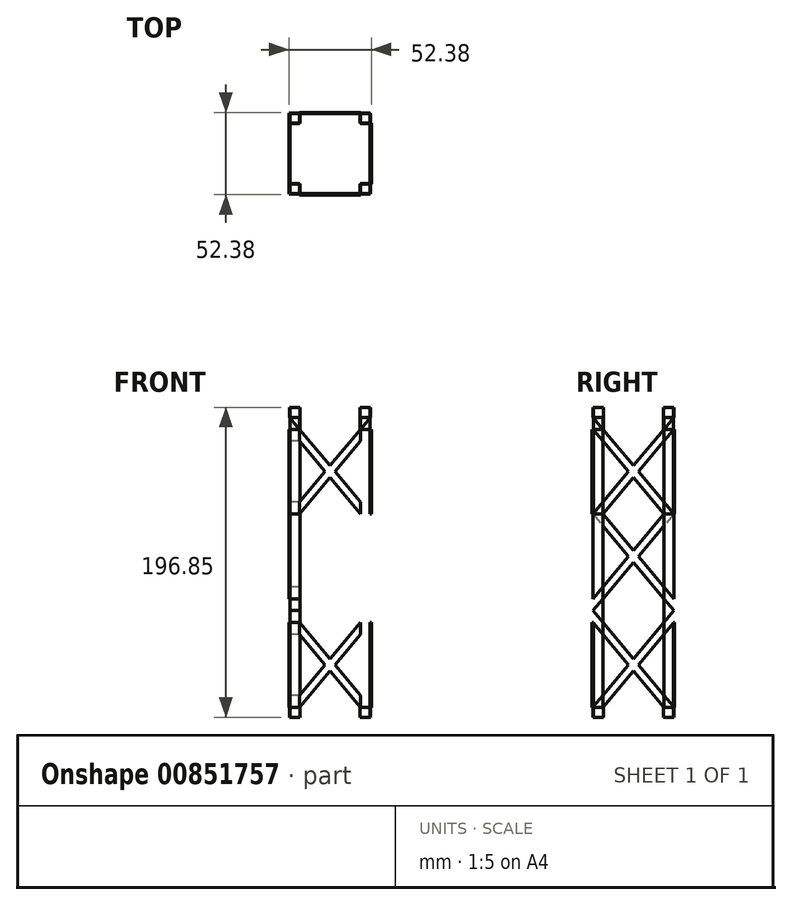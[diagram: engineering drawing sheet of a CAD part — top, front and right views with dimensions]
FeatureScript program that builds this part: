
annotation { "Feature Type Name" : "Feature", "Feature Type Description" : "" }
export const myFeature = defineFeature(function(context is Context, id is Id, definition is map)
    precondition{}
    {
        {
            var Q0;
            Q0=qCreatedBy(makeId("Front.planeOp"),FACE);
            var sketch = newSketch(context, id + "F0", { "sketchPlane" : qUnion([Q0])});
            skLineSegment(sketch, "E0", {"start": v(0, 0) * mm, "end": v(0, 196.85) * mm, "construction": true});
            skSolve(sketch);
        }
        {
            var Q0;
            Q0=qCreatedBy(makeId("Top.planeOp"),FACE);
            var sketch = newSketch(context, id + "F1", { "sketchPlane" : qUnion([Q0])});
            skLineSegment(sketch, "E1", {"start": v(0, 0) * mm, "end": v(-152.4, 0) * mm, "construction": true});
            skLineSegment(sketch, "E2", {"start": v(0, 0) * mm, "end": v(0, 152.4) * mm, "construction": true});
            skPoint(sketch, "E3", {"position": v(-25.4, 25.4) * mm});
            skPoint(sketch, "E4.MirrorP", {"position": v(-25.4, -25.4) * mm});
            skPoint(sketch, "E5.MirrorP", {"position": v(25.4, 25.4) * mm});
            skPoint(sketch, "E6.MirrorP", {"position": v(25.4, -25.4) * mm});
            skLineSegment(sketch, "E7", {"start": v(-25.4, 25.4) * mm, "end": v(-25.4, -25.4) * mm});
            skSolve(sketch);
        }
        {
            var Q0;
            Q0=sQuery(id+"F1.wireOp",EDGE,"E7");
            var Q1;
            Q1=qCreatedBy(makeId("Top.planeOp"),FACE);
            cPlane(context, id + "F2", {"entities" : qUnion([Q0, Q1]), "cplaneType" : CPlaneType.LINE_ANGLE, "offset" : 25.4 * mm, "angle" : 90 * degree, "width" : 152.4 * mm, "height" : 152.4 * mm});
        }
        {
            var Q0;
            Q0=qCreatedBy(id+"F2.planeOp",FACE);
            var sketch = newSketch(context, id + "F3", { "sketchPlane" : qUnion([Q0])});
            skLineSegment(sketch, "E8", {"start": v(-25.74, 0) * mm, "end": v(-25.74, 196.85) * mm});
            skLineSegment(sketch, "E9", {"start": v(-25.74, 196.85) * mm, "end": v(-19.39, 196.85) * mm});
            skLineSegment(sketch, "E10", {"start": v(-19.39, 196.85) * mm, "end": v(-19.39, 0) * mm});
            skLineSegment(sketch, "E11", {"start": v(-19.39, 0) * mm, "end": v(-25.74, 0) * mm});
            skLineSegment(sketch, "E12.MirrorCS", {"start": v(19.39, 0) * mm, "end": v(25.74, 0) * mm});
            skLineSegment(sketch, "E13.MirrorCS", {"start": v(25.74, 196.85) * mm, "end": v(19.39, 196.85) * mm});
            skLineSegment(sketch, "E14.MirrorCS", {"start": v(19.39, 196.85) * mm, "end": v(19.39, 0) * mm});
            skLineSegment(sketch, "E15.MirrorCS", {"start": v(25.74, 0) * mm, "end": v(25.74, 196.85) * mm});
            skLineSegment(sketch, "E16", {"start": v(25.74, 98.43) * mm, "end": v(-121.27, 98.43) * mm, "construction": true});
            skLineSegment(sketch, "E17", {"start": v(35.18, 190.5) * mm, "end": v(-76.67, 190.5) * mm, "construction": true});
            skLineSegment(sketch, "E18", {"start": v(34.82, 6.35) * mm, "end": v(-83.5, 6.35) * mm, "construction": true});
            skLineSegment(sketch, "E19", {"start": v(34.1, 129.12) * mm, "end": v(-115.16, 129.12) * mm, "construction": true});
            skLineSegment(sketch, "E20.MirrorCS", {"start": v(34.1, 67.73) * mm, "end": v(-115.16, 67.73) * mm, "construction": true});
            skLineSegment(sketch, "E21", {"start": v(19.39, 129.12) * mm, "end": v(-25.74, 75.3) * mm});
            skLineSegment(sketch, "E22", {"start": v(25.74, 129.12) * mm, "end": v(-25.74, 67.73) * mm});
            skLineSegment(sketch, "E23", {"start": v(25.74, 129.12) * mm, "end": v(19.39, 129.12) * mm});
            skLineSegment(sketch, "E24", {"start": v(-25.74, 75.3) * mm, "end": v(-25.74, 67.73) * mm});
            skLineSegment(sketch, "E25", {"start": v(-19.39, 129.12) * mm, "end": v(25.74, 75.3) * mm});
            skLineSegment(sketch, "E26", {"start": v(-25.74, 129.12) * mm, "end": v(25.74, 67.73) * mm});
            skLineSegment(sketch, "E27", {"start": v(-19.39, 129.12) * mm, "end": v(-25.74, 129.12) * mm});
            skLineSegment(sketch, "E28", {"start": v(25.74, 75.3) * mm, "end": v(25.74, 67.73) * mm});
            skLineSegment(sketch, "E29.MirrorCS", {"start": v(-25.74, 182.93) * mm, "end": v(-25.74, 190.5) * mm});
            skLineSegment(sketch, "E30.MirrorCS", {"start": v(19.39, 129.12) * mm, "end": v(-25.74, 182.93) * mm});
            skLineSegment(sketch, "E31.MirrorCS", {"start": v(25.74, 182.93) * mm, "end": v(25.74, 190.5) * mm});
            skLineSegment(sketch, "E32.MirrorCS", {"start": v(25.74, 129.12) * mm, "end": v(-25.74, 190.5) * mm});
            skLineSegment(sketch, "E33.MirrorCS", {"start": v(-19.39, 129.12) * mm, "end": v(25.74, 182.93) * mm});
            skLineSegment(sketch, "E34.MirrorCS", {"start": v(-25.74, 129.12) * mm, "end": v(25.74, 190.5) * mm});
            skLineSegment(sketch, "E35.MirrorCS", {"start": v(34.1, 190.5) * mm, "end": v(-115.16, 190.5) * mm, "construction": true});
            skLineSegment(sketch, "E36.MirrorCS", {"start": v(25.74, 6.35) * mm, "end": v(19.39, 6.35) * mm});
            skLineSegment(sketch, "E37.MirrorCS", {"start": v(-19.39, 6.35) * mm, "end": v(-25.74, 6.35) * mm});
            skLineSegment(sketch, "E38.MirrorCS", {"start": v(25.74, 60.16) * mm, "end": v(25.74, 67.73) * mm});
            skLineSegment(sketch, "E39.MirrorCS", {"start": v(-25.74, 60.16) * mm, "end": v(-25.74, 67.73) * mm});
            skLineSegment(sketch, "E40.MirrorCS", {"start": v(-25.74, 6.35) * mm, "end": v(25.74, 67.73) * mm});
            skLineSegment(sketch, "E41.MirrorCS", {"start": v(19.39, 6.35) * mm, "end": v(-25.74, 60.16) * mm});
            skLineSegment(sketch, "E42.MirrorCS", {"start": v(25.74, 6.35) * mm, "end": v(-25.74, 67.73) * mm});
            skLineSegment(sketch, "E43.MirrorCS", {"start": v(-19.39, 6.35) * mm, "end": v(25.74, 60.16) * mm});
            skSolve(sketch);
        }
        {
            var Q0;
            Q0=makeQuery(id+"F3.imprint","IMPRINT",FACE,{"disambiguationData":[TD([[makeQuery(id+"F3.imprint","IMPRINT",EDGE,{"derivedFrom":sQuery(id+"F3.wireOp",EDGE,"E11")}),-1.0]])]});
            var Q1;
            Q1=makeQuery(id+"F3.imprint","IMPRINT",FACE,{"disambiguationData":[TD([[makeQuery(id+"F3.imprint","IMPRINT",EDGE,{"derivedFrom":sQuery(id+"F3.wireOp",EDGE,"E12.MirrorCS")}),1.0]])]});
            var Q2;
            {var subQ0=sQuery(id+"F3.wireOp",EDGE,"E22");var subQ5=sQuery(id+"F3.wireOp",EDGE,"E14.MirrorCS");var subQ6=makeQuery(id+"F3.imprint","INTERSECT",VERTEX,{"derivedFrom":[subQ5,subQ0]});Q2=makeQuery(id+"F3.imprint","IMPRINT",FACE,{"disambiguationData":[TD([[makeQuery(id+"F3.imprint","IMPRINT",EDGE,{"disambiguationData":[TD([[subQ6,-1.0]])],"derivedFrom":subQ5}),1.0]])]});}
            var Q3;
            {var subQ3=sQuery(id+"F3.wireOp",EDGE,"E26");var subQ5=sQuery(id+"F3.wireOp",EDGE,"E10");var subQ7=makeQuery(id+"F3.imprint","INTERSECT",VERTEX,{"derivedFrom":[subQ5,subQ3]});Q3=makeQuery(id+"F3.imprint","IMPRINT",FACE,{"disambiguationData":[TD([[makeQuery(id+"F3.imprint","IMPRINT",EDGE,{"disambiguationData":[TD([[subQ7,-1.0]])],"derivedFrom":subQ5}),-1.0]])]});}
            var Q4;
            {var subQ0=sQuery(id+"F3.wireOp",EDGE,"E9");Q4=makeQuery(id+"F3.imprint","IMPRINT",FACE,{"disambiguationData":[TD([[makeQuery(id+"F3.imprint","IMPRINT",EDGE,{"derivedFrom":subQ0}),-1.0]])]});}
            var Q5;
            {var subQ0=sQuery(id+"F3.wireOp",EDGE,"E13.MirrorCS");Q5=makeQuery(id+"F3.imprint","IMPRINT",FACE,{"disambiguationData":[TD([[makeQuery(id+"F3.imprint","IMPRINT",EDGE,{"derivedFrom":subQ0}),1.0]])]});}
            var Q6;
            {var subQ0=sQuery(id+"F3.wireOp",EDGE,"E27");Q6=makeQuery(id+"F3.imprint","IMPRINT",FACE,{"disambiguationData":[TD([[makeQuery(id+"F3.imprint","IMPRINT",EDGE,{"derivedFrom":subQ0}),1.0]])]});}
            var Q7;
            {var subQ5=sQuery(id+"F3.wireOp",EDGE,"E24");Q7=makeQuery(id+"F3.imprint","IMPRINT",FACE,{"disambiguationData":[TD([[makeQuery(id+"F3.imprint","IMPRINT",EDGE,{"derivedFrom":subQ5}),1.0]])]});}
            var Q8;
            {var subQ0=sQuery(id+"F3.wireOp",EDGE,"E23");Q8=makeQuery(id+"F3.imprint","IMPRINT",FACE,{"disambiguationData":[TD([[makeQuery(id+"F3.imprint","IMPRINT",EDGE,{"derivedFrom":subQ0}),1.0]])]});}
            var Q9;
            {var subQ5=sQuery(id+"F3.wireOp",EDGE,"E28");Q9=makeQuery(id+"F3.imprint","IMPRINT",FACE,{"disambiguationData":[TD([[makeQuery(id+"F3.imprint","IMPRINT",EDGE,{"derivedFrom":subQ5}),-1.0]])]});}
            var Q10;
            {var subQ3=sQuery(id+"F3.wireOp",EDGE,"E30.MirrorCS");var subQ5=sQuery(id+"F3.wireOp",EDGE,"E10");var subQ6=makeQuery(id+"F3.imprint","INTERSECT",VERTEX,{"derivedFrom":[subQ5,subQ3]});Q10=makeQuery(id+"F3.imprint","IMPRINT",FACE,{"disambiguationData":[TD([[makeQuery(id+"F3.imprint","IMPRINT",EDGE,{"disambiguationData":[TD([[subQ6,-1.0]])],"derivedFrom":subQ5}),-1.0]])]});}
            var Q11;
            {var subQ5=sQuery(id+"F3.wireOp",EDGE,"E29.MirrorCS");Q11=makeQuery(id+"F3.imprint","IMPRINT",FACE,{"disambiguationData":[TD([[makeQuery(id+"F3.imprint","IMPRINT",EDGE,{"derivedFrom":subQ5}),-1.0]])]});}
            var Q12;
            {var subQ5=sQuery(id+"F3.wireOp",EDGE,"E31.MirrorCS");Q12=makeQuery(id+"F3.imprint","IMPRINT",FACE,{"disambiguationData":[TD([[makeQuery(id+"F3.imprint","IMPRINT",EDGE,{"derivedFrom":subQ5}),1.0]])]});}
            var Q13;
            {var subQ3=sQuery(id+"F3.wireOp",EDGE,"E33.MirrorCS");var subQ5=sQuery(id+"F3.wireOp",EDGE,"E14.MirrorCS");var subQ6=makeQuery(id+"F3.imprint","INTERSECT",VERTEX,{"derivedFrom":[subQ5,subQ3]});Q13=makeQuery(id+"F3.imprint","IMPRINT",FACE,{"disambiguationData":[TD([[makeQuery(id+"F3.imprint","IMPRINT",EDGE,{"disambiguationData":[TD([[subQ6,-1.0]])],"derivedFrom":subQ5}),1.0]])]});}
            var Q14;
            {var subQ0=sQuery(id+"F3.wireOp",EDGE,"E23");Q14=makeQuery(id+"F3.imprint","IMPRINT",FACE,{"disambiguationData":[TD([[makeQuery(id+"F3.imprint","IMPRINT",EDGE,{"derivedFrom":subQ0}),-1.0]])]});}
            var Q15;
            {var subQ0=sQuery(id+"F3.wireOp",EDGE,"E23");Q15=makeQuery(id+"F3.imprint","IMPRINT",FACE,{"disambiguationData":[TD([[makeQuery(id+"F3.imprint","IMPRINT",EDGE,{"derivedFrom":subQ0}),1.0]])]});}
            var Q16;
            {var subQ0=sQuery(id+"F3.wireOp",EDGE,"E27");Q16=makeQuery(id+"F3.imprint","IMPRINT",FACE,{"disambiguationData":[TD([[makeQuery(id+"F3.imprint","IMPRINT",EDGE,{"derivedFrom":subQ0}),1.0]])]});}
            var Q17;
            {var subQ0=sQuery(id+"F3.wireOp",EDGE,"E27");Q17=makeQuery(id+"F3.imprint","IMPRINT",FACE,{"disambiguationData":[TD([[makeQuery(id+"F3.imprint","IMPRINT",EDGE,{"derivedFrom":subQ0}),-1.0]])]});}
            var Q18;
            {var subQ5=sQuery(id+"F3.wireOp",EDGE,"E38.MirrorCS");Q18=makeQuery(id+"F3.imprint","IMPRINT",FACE,{"disambiguationData":[TD([[makeQuery(id+"F3.imprint","IMPRINT",EDGE,{"derivedFrom":subQ5}),1.0]])]});}
            var Q19;
            {var subQ3=sQuery(id+"F3.wireOp",EDGE,"E43.MirrorCS");var subQ5=sQuery(id+"F3.wireOp",EDGE,"E14.MirrorCS");var subQ6=makeQuery(id+"F3.imprint","INTERSECT",VERTEX,{"derivedFrom":[subQ5,subQ3]});Q19=makeQuery(id+"F3.imprint","IMPRINT",FACE,{"disambiguationData":[TD([[makeQuery(id+"F3.imprint","IMPRINT",EDGE,{"disambiguationData":[TD([[subQ6,-1.0]])],"derivedFrom":subQ5}),1.0]])]});}
            var Q20;
            {var subQ0=sQuery(id+"F3.wireOp",EDGE,"E22");var subQ1=sQuery(id+"F3.wireOp",EDGE,"E10");var subQ2=makeQuery(id+"F3.imprint","INTERSECT",VERTEX,{"derivedFrom":[subQ1,subQ0]});Q20=makeQuery(id+"F3.imprint","IMPRINT",FACE,{"disambiguationData":[TD([[makeQuery(id+"F3.imprint","IMPRINT",EDGE,{"disambiguationData":[TD([[subQ2,-1.0]])],"derivedFrom":subQ1}),-1.0]])]});}
            var Q21;
            {var subQ5=sQuery(id+"F3.wireOp",EDGE,"E39.MirrorCS");Q21=makeQuery(id+"F3.imprint","IMPRINT",FACE,{"disambiguationData":[TD([[makeQuery(id+"F3.imprint","IMPRINT",EDGE,{"derivedFrom":subQ5}),-1.0]])]});}
            var Q22;
            {var subQ3=sQuery(id+"F3.wireOp",EDGE,"E41.MirrorCS");var subQ5=sQuery(id+"F3.wireOp",EDGE,"E10");var subQ6=makeQuery(id+"F3.imprint","INTERSECT",VERTEX,{"derivedFrom":[subQ5,subQ3]});Q22=makeQuery(id+"F3.imprint","IMPRINT",FACE,{"disambiguationData":[TD([[makeQuery(id+"F3.imprint","IMPRINT",EDGE,{"disambiguationData":[TD([[subQ6,-1.0]])],"derivedFrom":subQ5}),-1.0]])]});}
            var Q23;
            {var subQ0=sQuery(id+"F3.wireOp",EDGE,"E36.MirrorCS");Q23=makeQuery(id+"F3.imprint","IMPRINT",FACE,{"disambiguationData":[TD([[makeQuery(id+"F3.imprint","IMPRINT",EDGE,{"derivedFrom":subQ0}),-1.0]])]});}
            var Q24;
            {var subQ0=sQuery(id+"F3.wireOp",EDGE,"E26");var subQ1=sQuery(id+"F3.wireOp",EDGE,"E14.MirrorCS");var subQ2=makeQuery(id+"F3.imprint","INTERSECT",VERTEX,{"derivedFrom":[subQ1,subQ0]});Q24=makeQuery(id+"F3.imprint","IMPRINT",FACE,{"disambiguationData":[TD([[makeQuery(id+"F3.imprint","IMPRINT",EDGE,{"disambiguationData":[TD([[subQ2,-1.0]])],"derivedFrom":subQ1}),1.0]])]});}
            var Q25;
            {var subQ0=sQuery(id+"F3.wireOp",EDGE,"E37.MirrorCS");Q25=makeQuery(id+"F3.imprint","IMPRINT",FACE,{"disambiguationData":[TD([[makeQuery(id+"F3.imprint","IMPRINT",EDGE,{"derivedFrom":subQ0}),-1.0]])]});}
            extrude(context, id + "F4", {"entities" : qUnion([Q0, Q1, Q2, Q3, Q4, Q5, Q6, Q7, Q8, Q9, Q10, Q11, Q12, Q13, Q14, Q15, Q16, Q17, Q18, Q19, Q20, Q21, Q22, Q23, Q24, Q25]), "depth" : 6.35 * mm, "offsetDistance" : 25.4 * mm});
        }
        {
            var Q0;
            {var subQ0=sQuery(id+"F3.wireOp",EDGE,"E25");var subQ5=sQuery(id+"F3.wireOp",EDGE,"E21");var subQ6=makeQuery(id+"F3.imprint","INTERSECT",VERTEX,{"derivedFrom":[subQ5,subQ0]});Q0=makeQuery(id+"F3.imprint","IMPRINT",FACE,{"disambiguationData":[TD([[makeQuery(id+"F3.imprint","IMPRINT",EDGE,{"disambiguationData":[TD([[subQ6,-1.0]])],"derivedFrom":subQ5}),-1.0]])]});}
            var Q1;
            {var subQ0=sQuery(id+"F3.wireOp",EDGE,"E27");Q1=makeQuery(id+"F3.imprint","IMPRINT",FACE,{"disambiguationData":[TD([[makeQuery(id+"F3.imprint","IMPRINT",EDGE,{"derivedFrom":subQ0}),1.0]])]});}
            var Q2;
            {var subQ0=sQuery(id+"F3.wireOp",EDGE,"E22");var subQ1=sQuery(id+"F3.wireOp",EDGE,"E10");var subQ2=makeQuery(id+"F3.imprint","INTERSECT",VERTEX,{"derivedFrom":[subQ1,subQ0]});Q2=makeQuery(id+"F3.imprint","IMPRINT",FACE,{"disambiguationData":[TD([[makeQuery(id+"F3.imprint","IMPRINT",EDGE,{"disambiguationData":[TD([[subQ2,1.0]])],"derivedFrom":subQ1}),1.0]])]});}
            var Q3;
            {var subQ5=sQuery(id+"F3.wireOp",EDGE,"E24");Q3=makeQuery(id+"F3.imprint","IMPRINT",FACE,{"disambiguationData":[TD([[makeQuery(id+"F3.imprint","IMPRINT",EDGE,{"derivedFrom":subQ5}),1.0]])]});}
            var Q4;
            {var subQ0=sQuery(id+"F3.wireOp",EDGE,"E26");var subQ1=sQuery(id+"F3.wireOp",EDGE,"E14.MirrorCS");var subQ2=makeQuery(id+"F3.imprint","INTERSECT",VERTEX,{"derivedFrom":[subQ1,subQ0]});Q4=makeQuery(id+"F3.imprint","IMPRINT",FACE,{"disambiguationData":[TD([[makeQuery(id+"F3.imprint","IMPRINT",EDGE,{"disambiguationData":[TD([[subQ2,1.0]])],"derivedFrom":subQ1}),-1.0]])]});}
            var Q5;
            {var subQ5=sQuery(id+"F3.wireOp",EDGE,"E28");Q5=makeQuery(id+"F3.imprint","IMPRINT",FACE,{"disambiguationData":[TD([[makeQuery(id+"F3.imprint","IMPRINT",EDGE,{"derivedFrom":subQ5}),-1.0]])]});}
            var Q6;
            {var subQ0=sQuery(id+"F3.wireOp",EDGE,"E25");var subQ1=sQuery(id+"F3.wireOp",EDGE,"E21");var subQ2=makeQuery(id+"F3.imprint","INTERSECT",VERTEX,{"derivedFrom":[subQ1,subQ0]});Q6=makeQuery(id+"F3.imprint","IMPRINT",FACE,{"disambiguationData":[TD([[makeQuery(id+"F3.imprint","IMPRINT",EDGE,{"disambiguationData":[TD([[subQ2,-1.0]])],"derivedFrom":subQ1}),1.0]])]});}
            var Q7;
            {var subQ0=sQuery(id+"F3.wireOp",EDGE,"E23");Q7=makeQuery(id+"F3.imprint","IMPRINT",FACE,{"disambiguationData":[TD([[makeQuery(id+"F3.imprint","IMPRINT",EDGE,{"derivedFrom":subQ0}),1.0]])]});}
            var Q8;
            {var subQ1=sQuery(id+"F3.wireOp",EDGE,"E14.MirrorCS");var subQ3=sQuery(id+"F3.wireOp",EDGE,"E22");var subQ4=makeQuery(id+"F3.imprint","INTERSECT",VERTEX,{"derivedFrom":[subQ1,subQ3]});Q8=makeQuery(id+"F3.imprint","IMPRINT",FACE,{"disambiguationData":[TD([[makeQuery(id+"F3.imprint","IMPRINT",EDGE,{"disambiguationData":[TD([[subQ4,-1.0]])],"derivedFrom":subQ3}),-1.0]])]});}
            var Q9;
            {var subQ5=sQuery(id+"F3.wireOp",EDGE,"E31.MirrorCS");Q9=makeQuery(id+"F3.imprint","IMPRINT",FACE,{"disambiguationData":[TD([[makeQuery(id+"F3.imprint","IMPRINT",EDGE,{"derivedFrom":subQ5}),1.0]])]});}
            var Q10;
            {var subQ0=sQuery(id+"F3.wireOp",EDGE,"E34.MirrorCS");var subQ1=sQuery(id+"F3.wireOp",EDGE,"E14.MirrorCS");var subQ2=makeQuery(id+"F3.imprint","INTERSECT",VERTEX,{"derivedFrom":[subQ1,subQ0]});Q10=makeQuery(id+"F3.imprint","IMPRINT",FACE,{"disambiguationData":[TD([[makeQuery(id+"F3.imprint","IMPRINT",EDGE,{"disambiguationData":[TD([[subQ2,-1.0]])],"derivedFrom":subQ1}),-1.0]])]});}
            var Q11;
            {var subQ0=sQuery(id+"F3.wireOp",EDGE,"E32.MirrorCS");var subQ1=sQuery(id+"F3.wireOp",EDGE,"E10");var subQ2=makeQuery(id+"F3.imprint","INTERSECT",VERTEX,{"derivedFrom":[subQ1,subQ0]});Q11=makeQuery(id+"F3.imprint","IMPRINT",FACE,{"disambiguationData":[TD([[makeQuery(id+"F3.imprint","IMPRINT",EDGE,{"disambiguationData":[TD([[subQ2,-1.0]])],"derivedFrom":subQ1}),1.0]])]});}
            var Q12;
            {var subQ5=sQuery(id+"F3.wireOp",EDGE,"E29.MirrorCS");Q12=makeQuery(id+"F3.imprint","IMPRINT",FACE,{"disambiguationData":[TD([[makeQuery(id+"F3.imprint","IMPRINT",EDGE,{"derivedFrom":subQ5}),-1.0]])]});}
            var Q13;
            {var subQ0=sQuery(id+"F3.wireOp",EDGE,"E33.MirrorCS");var subQ1=sQuery(id+"F3.wireOp",EDGE,"E30.MirrorCS");var subQ2=makeQuery(id+"F3.imprint","INTERSECT",VERTEX,{"derivedFrom":[subQ1,subQ0]});Q13=makeQuery(id+"F3.imprint","IMPRINT",FACE,{"disambiguationData":[TD([[makeQuery(id+"F3.imprint","IMPRINT",EDGE,{"disambiguationData":[TD([[subQ2,-1.0]])],"derivedFrom":subQ1}),-1.0]])]});}
            var Q14;
            {var subQ1=sQuery(id+"F3.wireOp",EDGE,"E14.MirrorCS");var subQ3=sQuery(id+"F3.wireOp",EDGE,"E32.MirrorCS");var subQ4=makeQuery(id+"F3.imprint","INTERSECT",VERTEX,{"derivedFrom":[subQ1,subQ3]});Q14=makeQuery(id+"F3.imprint","IMPRINT",FACE,{"disambiguationData":[TD([[makeQuery(id+"F3.imprint","IMPRINT",EDGE,{"disambiguationData":[TD([[subQ4,-1.0]])],"derivedFrom":subQ3}),1.0]])]});}
            var Q15;
            {var subQ0=sQuery(id+"F3.wireOp",EDGE,"E27");Q15=makeQuery(id+"F3.imprint","IMPRINT",FACE,{"disambiguationData":[TD([[makeQuery(id+"F3.imprint","IMPRINT",EDGE,{"derivedFrom":subQ0}),-1.0]])]});}
            var Q16;
            {var subQ0=sQuery(id+"F3.wireOp",EDGE,"E27");Q16=makeQuery(id+"F3.imprint","IMPRINT",FACE,{"disambiguationData":[TD([[makeQuery(id+"F3.imprint","IMPRINT",EDGE,{"derivedFrom":subQ0}),1.0]])]});}
            var Q17;
            {var subQ0=sQuery(id+"F3.wireOp",EDGE,"E23");Q17=makeQuery(id+"F3.imprint","IMPRINT",FACE,{"disambiguationData":[TD([[makeQuery(id+"F3.imprint","IMPRINT",EDGE,{"derivedFrom":subQ0}),-1.0]])]});}
            var Q18;
            {var subQ0=sQuery(id+"F3.wireOp",EDGE,"E23");Q18=makeQuery(id+"F3.imprint","IMPRINT",FACE,{"disambiguationData":[TD([[makeQuery(id+"F3.imprint","IMPRINT",EDGE,{"derivedFrom":subQ0}),1.0]])]});}
            var Q19;
            {var subQ0=sQuery(id+"F3.wireOp",EDGE,"E33.MirrorCS");var subQ5=sQuery(id+"F3.wireOp",EDGE,"E30.MirrorCS");var subQ6=makeQuery(id+"F3.imprint","INTERSECT",VERTEX,{"derivedFrom":[subQ5,subQ0]});Q19=makeQuery(id+"F3.imprint","IMPRINT",FACE,{"disambiguationData":[TD([[makeQuery(id+"F3.imprint","IMPRINT",EDGE,{"disambiguationData":[TD([[subQ6,-1.0]])],"derivedFrom":subQ5}),1.0]])]});}
            var Q20;
            {var subQ5=sQuery(id+"F3.wireOp",EDGE,"E39.MirrorCS");Q20=makeQuery(id+"F3.imprint","IMPRINT",FACE,{"disambiguationData":[TD([[makeQuery(id+"F3.imprint","IMPRINT",EDGE,{"derivedFrom":subQ5}),-1.0]])]});}
            var Q21;
            {var subQ0=sQuery(id+"F3.wireOp",EDGE,"E40.MirrorCS");var subQ1=sQuery(id+"F3.wireOp",EDGE,"E14.MirrorCS");var subQ2=makeQuery(id+"F3.imprint","INTERSECT",VERTEX,{"derivedFrom":[subQ1,subQ0]});Q21=makeQuery(id+"F3.imprint","IMPRINT",FACE,{"disambiguationData":[TD([[makeQuery(id+"F3.imprint","IMPRINT",EDGE,{"disambiguationData":[TD([[subQ2,-1.0]])],"derivedFrom":subQ1}),-1.0]])]});}
            var Q22;
            {var subQ0=sQuery(id+"F3.wireOp",EDGE,"E42.MirrorCS");var subQ1=sQuery(id+"F3.wireOp",EDGE,"E10");var subQ2=makeQuery(id+"F3.imprint","INTERSECT",VERTEX,{"derivedFrom":[subQ1,subQ0]});Q22=makeQuery(id+"F3.imprint","IMPRINT",FACE,{"disambiguationData":[TD([[makeQuery(id+"F3.imprint","IMPRINT",EDGE,{"disambiguationData":[TD([[subQ2,-1.0]])],"derivedFrom":subQ1}),1.0]])]});}
            var Q23;
            {var subQ1=sQuery(id+"F3.wireOp",EDGE,"E10");var subQ3=sQuery(id+"F3.wireOp",EDGE,"E40.MirrorCS");var subQ4=makeQuery(id+"F3.imprint","INTERSECT",VERTEX,{"derivedFrom":[subQ1,subQ3]});Q23=makeQuery(id+"F3.imprint","IMPRINT",FACE,{"disambiguationData":[TD([[makeQuery(id+"F3.imprint","IMPRINT",EDGE,{"disambiguationData":[TD([[subQ4,-1.0]])],"derivedFrom":subQ3}),-1.0]])]});}
            var Q24;
            {var subQ0=sQuery(id+"F3.wireOp",EDGE,"E41.MirrorCS");var subQ1=sQuery(id+"F3.wireOp",EDGE,"E40.MirrorCS");var subQ2=makeQuery(id+"F3.imprint","INTERSECT",VERTEX,{"derivedFrom":[subQ1,subQ0]});Q24=makeQuery(id+"F3.imprint","IMPRINT",FACE,{"disambiguationData":[TD([[makeQuery(id+"F3.imprint","IMPRINT",EDGE,{"disambiguationData":[TD([[subQ2,-1.0]])],"derivedFrom":subQ1}),-1.0]])]});}
            var Q25;
            {var subQ5=sQuery(id+"F3.wireOp",EDGE,"E38.MirrorCS");Q25=makeQuery(id+"F3.imprint","IMPRINT",FACE,{"disambiguationData":[TD([[makeQuery(id+"F3.imprint","IMPRINT",EDGE,{"derivedFrom":subQ5}),1.0]])]});}
            var Q26;
            {var subQ1=sQuery(id+"F3.wireOp",EDGE,"E14.MirrorCS");var subQ3=sQuery(id+"F3.wireOp",EDGE,"E42.MirrorCS");var subQ4=makeQuery(id+"F3.imprint","INTERSECT",VERTEX,{"derivedFrom":[subQ1,subQ3]});Q26=makeQuery(id+"F3.imprint","IMPRINT",FACE,{"disambiguationData":[TD([[makeQuery(id+"F3.imprint","IMPRINT",EDGE,{"disambiguationData":[TD([[subQ4,-1.0]])],"derivedFrom":subQ3}),1.0]])]});}
            var Q27;
            {var subQ0=sQuery(id+"F3.wireOp",EDGE,"E37.MirrorCS");Q27=makeQuery(id+"F3.imprint","IMPRINT",FACE,{"disambiguationData":[TD([[makeQuery(id+"F3.imprint","IMPRINT",EDGE,{"derivedFrom":subQ0}),-1.0]])]});}
            var Q28;
            {var subQ0=sQuery(id+"F3.wireOp",EDGE,"E36.MirrorCS");Q28=makeQuery(id+"F3.imprint","IMPRINT",FACE,{"disambiguationData":[TD([[makeQuery(id+"F3.imprint","IMPRINT",EDGE,{"derivedFrom":subQ0}),-1.0]])]});}
            extrude(context, id + "F5", {"entities" : qUnion([Q0, Q1, Q2, Q3, Q4, Q5, Q6, Q7, Q8, Q9, Q10, Q11, Q12, Q13, Q14, Q15, Q16, Q17, Q18, Q19, Q20, Q21, Q22, Q23, Q24, Q25, Q26, Q27, Q28]), "oppositeDirection" : true, "depth" : 0.8 * mm, "offsetDistance" : 25.4 * mm});
        }
        {
            var Q0;
            Q0=makeQuery(id+"F4.opExtrude","SWEPT_BODY",BODY,{"disambiguationData":[OSD([sQuery(id+"F3.wireOp",EDGE,"E12.MirrorCS"),sQuery(id+"F3.wireOp",EDGE,"E13.MirrorCS"),sQuery(id+"F3.wireOp",EDGE,"E15.MirrorCS"),sQuery(id+"F3.wireOp",EDGE,"E14.MirrorCS"),sQuery(id+"F3.wireOp",EDGE,"E28"),sQuery(id+"F3.wireOp",EDGE,"E31.MirrorCS"),sQuery(id+"F3.wireOp",EDGE,"E38.MirrorCS")])]});
            var Q1;
            Q1=makeQuery(id+"F4.opExtrude","SWEPT_BODY",BODY,{"disambiguationData":[OSD([sQuery(id+"F3.wireOp",EDGE,"E11"),sQuery(id+"F3.wireOp",EDGE,"E9"),sQuery(id+"F3.wireOp",EDGE,"E8"),sQuery(id+"F3.wireOp",EDGE,"E10"),sQuery(id+"F3.wireOp",EDGE,"E24"),sQuery(id+"F3.wireOp",EDGE,"E29.MirrorCS"),sQuery(id+"F3.wireOp",EDGE,"E39.MirrorCS")])]});
            var Q2;
            Q2=makeQuery(id+"F5.opExtrude","SWEPT_BODY",BODY,{"disambiguationData":[OSD([sQuery(id+"F3.wireOp",EDGE,"E37.MirrorCS"),sQuery(id+"F3.wireOp",EDGE,"E36.MirrorCS"),sQuery(id+"F3.wireOp",EDGE,"E38.MirrorCS"),sQuery(id+"F3.wireOp",EDGE,"E40.MirrorCS"),sQuery(id+"F3.wireOp",EDGE,"E41.MirrorCS"),sQuery(id+"F3.wireOp",EDGE,"E42.MirrorCS"),sQuery(id+"F3.wireOp",EDGE,"E43.MirrorCS"),sQuery(id+"F3.wireOp",EDGE,"E39.MirrorCS")])]});
            var Q3;
            Q3=makeQuery(id+"F5.opExtrude","SWEPT_BODY",BODY,{"disambiguationData":[OSD([sQuery(id+"F3.wireOp",EDGE,"E21"),sQuery(id+"F3.wireOp",EDGE,"E22"),sQuery(id+"F3.wireOp",EDGE,"E25"),sQuery(id+"F3.wireOp",EDGE,"E26"),sQuery(id+"F3.wireOp",EDGE,"E24"),sQuery(id+"F3.wireOp",EDGE,"E28"),sQuery(id+"F3.wireOp",EDGE,"E30.MirrorCS"),sQuery(id+"F3.wireOp",EDGE,"E31.MirrorCS"),sQuery(id+"F3.wireOp",EDGE,"E32.MirrorCS"),sQuery(id+"F3.wireOp",EDGE,"E33.MirrorCS"),sQuery(id+"F3.wireOp",EDGE,"E29.MirrorCS"),sQuery(id+"F3.wireOp",EDGE,"E34.MirrorCS")])]});
            var Q4;
            Q4=sQuery(id+"F0.wireOp",EDGE,"E0");
            circularPattern(context, id + "F6", {"entities" : qUnion([Q0, Q1, Q2, Q3]), "axis" : qUnion([Q4]), "angle" : 360 * degree, "instanceCount" : 4, "equalSpace" : true});
        }
    });
